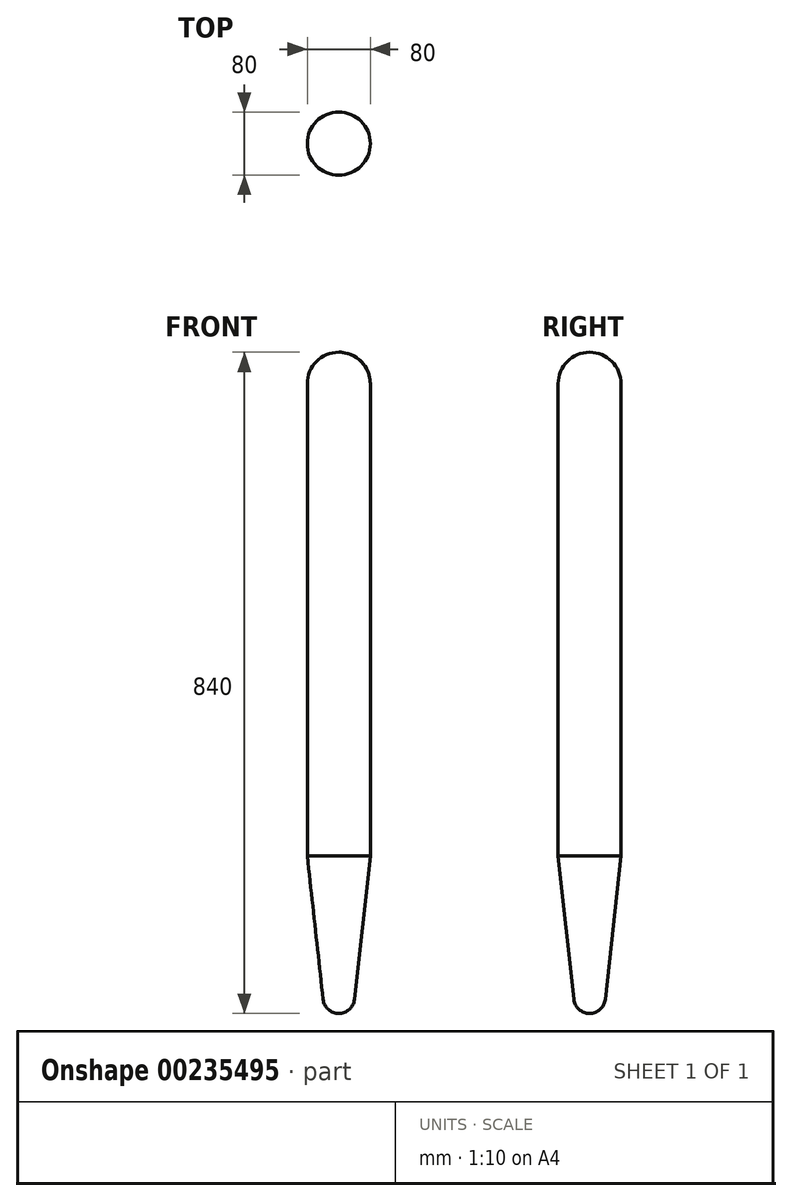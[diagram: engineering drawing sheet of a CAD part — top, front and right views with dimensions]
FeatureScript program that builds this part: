
annotation { "Feature Type Name" : "Feature", "Feature Type Description" : "" }
export const myFeature = defineFeature(function(context is Context, id is Id, definition is map)
    precondition{}
    {
        {
            var Q0;
            Q0=qCreatedBy(makeId("Front.planeOp"),FACE);
            var sketch = newSketch(context, id + "F0", { "sketchPlane" : qUnion([Q0])});
            skLineSegment(sketch, "E0", {"start": v(-40, 0) * mm, "end": v(-40, 600) * mm});
            skLineSegment(sketch, "E1", {"start": v(-40, 600) * mm, "end": v(40, 600) * mm});
            skLineSegment(sketch, "E2", {"start": v(40, 600) * mm, "end": v(40, 0) * mm});
            skLineSegment(sketch, "E3", {"start": v(40, 0) * mm, "end": v(-40, 0) * mm});
            skArc(sketch, "E4", {"start": v(-19.88, -182.2) * mm, "mid": v(0, -200) * mm, "end": v(19.88, -182.2) * mm});
            skLineSegment(sketch, "E5", {"start": v(-40, 0) * mm, "end": v(-19.88, -182.2) * mm});
            skLineSegment(sketch, "E6", {"start": v(40, 0) * mm, "end": v(19.88, -182.2) * mm});
            skLineSegment(sketch, "E7", {"start": v(0, -200) * mm, "end": v(0, 640) * mm});
            skPoint(sketch, "E7.startSnap0", {"position": v(0, -200) * mm});
            skArc(sketch, "E8", {"start": v(40, 600) * mm, "mid": v(0, 640) * mm, "end": v(-40, 600) * mm});
            skPoint(sketch, "E9.orphan", {"position": v(0, -261) * mm});
            skSolve(sketch);
        }
        {
            var Q0;
            {var subQ0=sQuery(id+"F0.wireOp",EDGE,"E0");Q0=makeQuery(id+"F0.imprint","IMPRINT",FACE,{"disambiguationData":[TD([[makeQuery(id+"F0.imprint","IMPRINT",EDGE,{"derivedFrom":subQ0}),-1.0]])]});}
            var Q1;
            {var subQ0=sQuery(id+"F0.wireOp",EDGE,"E8");var subQ3=sQuery(id+"F0.wireOp",EDGE,"E7");var subQ5=makeQuery(id+"F0.imprint","INTERSECT",VERTEX,{"derivedFrom":[subQ3,subQ0]});Q1=makeQuery(id+"F0.imprint","IMPRINT",FACE,{"disambiguationData":[TD([[makeQuery(id+"F0.imprint","IMPRINT",EDGE,{"disambiguationData":[TD([[subQ5,1.0]])],"derivedFrom":subQ3}),1.0]])]});}
            var Q2;
            {var subQ0=sQuery(id+"F0.wireOp",EDGE,"E5");Q2=makeQuery(id+"F0.imprint","IMPRINT",FACE,{"disambiguationData":[TD([[makeQuery(id+"F0.imprint","IMPRINT",EDGE,{"derivedFrom":subQ0}),1.0]])]});}
            var Q3;
            Q3=sQuery(id+"F0.wireOp",EDGE,"E7");
            revolve(context, id + "F1", {"entities" : qUnion([Q0, Q1, Q2]), "axis" : qUnion([Q3]), "revolveType" : RevolveType.FULL});
        }
    });
